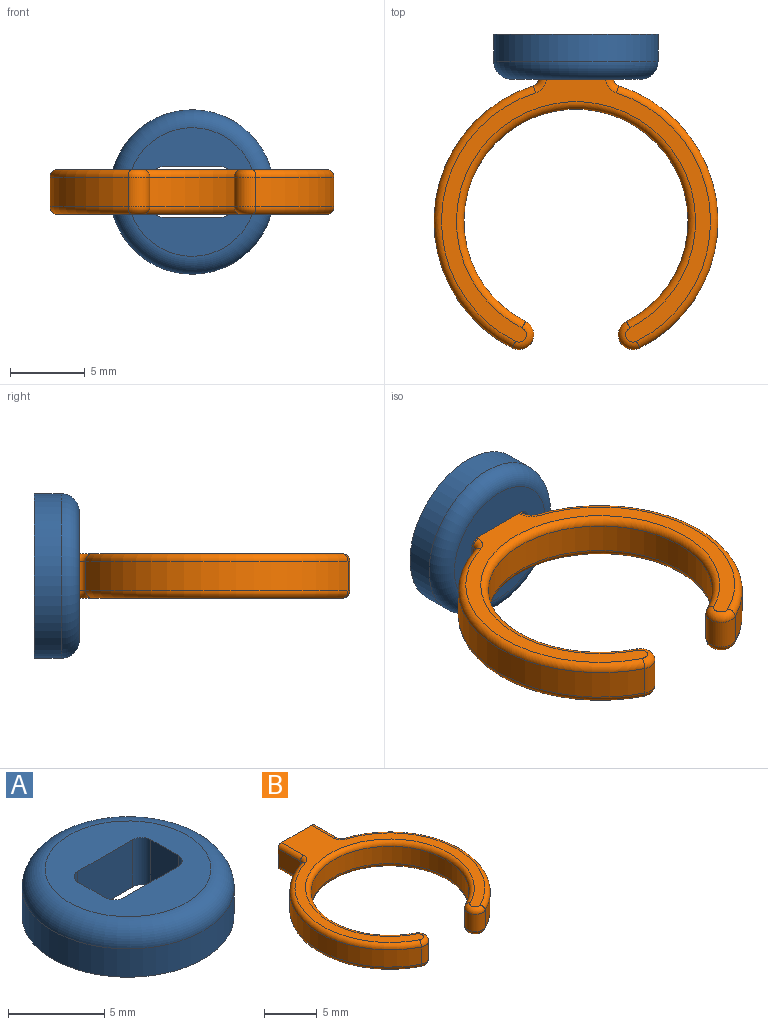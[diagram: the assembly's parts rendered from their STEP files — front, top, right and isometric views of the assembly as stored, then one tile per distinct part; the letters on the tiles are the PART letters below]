
ASSEMBLY  parts=2 mates=1
PART A: 12 faces, bbox 11.9x11.9x3 mm
  f0: plane 3x2mm, normal (1,0,0), area 6mm2, adj f5,f6,f8,f11
  f1: plane 4x3mm, normal (0,-1,0), area 12mm2, adj f5,f6,f8,f9
  f2: plane 3x2mm, normal (-1,0,0), area 6mm2, adj f5,f6,f9,f10
  f3: plane 4x3mm, normal (0,1,0), area 12mm2, adj f5,f6,f10,f11
  f4: cylinder r=5.5mm len=11mm, axis (0,0,-1), area 62.2mm2, adj f6,f7
  f5: plane 8.6x8.6mm, normal (0,0,1), area 40.5mm2, adj f0,f1,f2,f3,f7,f8,f9,f10
  f6: plane 11x11mm, normal (0,0,-1), area 77.4mm2, adj f0,f1,f2,f3,f4,f8,f9,f10
  f7: torus R=4.3mm, axis (0,0,1), area 60mm2, adj f4,f5
  f8: cylinder r=0.68mm len=3mm, axis (0,0,-1), area 3.2mm2, adj f0,f1,f5,f6
  f9: cylinder r=0.68mm len=3mm, axis (0,0,1), area 3.2mm2, adj f1,f2,f5,f6
  f10: cylinder r=0.68mm len=3mm, axis (0,0,-1), area 3.2mm2, adj f2,f3,f5,f6
  f11: cylinder r=0.68mm len=3mm, axis (0,0,1), area 3.2mm2, adj f0,f3,f5,f6
PART B: 30 faces, bbox 20.6x21.7x3 mm
  f0: plane 2.96x2mm, normal (-1,0,0), area 5.9mm2, adj f1,f7,f12,f21
  f1: cylinder r=0.5mm len=2mm, axis (0,0,-1), area 1.3mm2, adj f0,f2,f13,f22
  f2: cylinder r=9.5mm len=17.55mm, axis (0,0,-1), area 45mm2, adj f1,f10,f14,f23
  f3: cylinder r=7.5mm len=15mm, axis (0,0,-1), area 80.2mm2, adj f10,f11,f16,f25
  f4: cylinder r=9.5mm len=17.55mm, axis (0,0,-1), area 45mm2, adj f5,f11,f18,f27
  f5: cylinder r=0.5mm len=2mm, axis (0,0,-1), area 1.3mm2, adj f4,f6,f19,f28
  f6: plane 2.96x2mm, normal (1,0,0), area 5.9mm2, adj f5,f7,f20,f29
  f7: plane 5x3mm, normal (0,1,0), area 14.8mm2, adj f0,f6,f8,f9,f12,f20,f21,f29
  f8: plane 20.59x18mm, normal (0,0,1), area 60.8mm2, adj f7,f12,f13,f14,f15,f16,f17,f18
  f9: plane 20.59x18mm, normal (0,0,-1), area 60.8mm2, adj f7,f21,f22,f23,f24,f25,f26,f27
  f10: cylinder r=1mm len=2mm, axis (0,0,-1), area 6.3mm2, adj f2,f3,f15,f24
  f11: cylinder r=1mm len=2mm, axis (0,0,-1), area 6.3mm2, adj f3,f4,f17,f26
  f12: cylinder r=0.5mm len=2.96mm, axis (0,1,0), area 2.3mm2, adj f0,f7,f8,f13
  f13: torus R=1mm, axis (0,0,1), area 0.7mm2, adj f1,f8,f12,f14
  f14: torus R=9mm, axis (0,0,1), area 17.3mm2, adj f2,f8,f13,f15
  f15: torus R=0.5mm, axis (0,0,1), area 2mm2, adj f8,f10,f14,f16
  f16: torus R=8mm, axis (0,0,1), area 32.3mm2, adj f3,f8,f15,f17
  f17: torus R=0.5mm, axis (0,0,1), area 2mm2, adj f8,f11,f16,f18
  f18: torus R=9mm, axis (0,0,1), area 17.3mm2, adj f4,f8,f17,f19
  f19: torus R=1mm, axis (0,0,1), area 0.7mm2, adj f5,f8,f18,f20
  f20: cylinder r=0.5mm len=2.96mm, axis (0,-1,0), area 2.3mm2, adj f6,f7,f8,f19
  f21: cylinder r=0.5mm len=2.96mm, axis (0,-1,0), area 2.3mm2, adj f0,f7,f9,f22
  f22: torus R=1mm, axis (0,0,1), area 0.7mm2, adj f1,f9,f21,f23
  f23: torus R=9mm, axis (0,0,1), area 17.3mm2, adj f2,f9,f22,f24
  f24: torus R=0.5mm, axis (0,0,1), area 2mm2, adj f9,f10,f23,f25
  f25: torus R=8mm, axis (0,0,1), area 32.3mm2, adj f3,f9,f24,f26
  f26: torus R=0.5mm, axis (0,0,1), area 2mm2, adj f9,f11,f25,f27
  f27: torus R=9mm, axis (0,0,1), area 17.3mm2, adj f4,f9,f26,f28
  f28: torus R=1mm, axis (0,0,1), area 0.7mm2, adj f5,f9,f27,f29
  f29: cylinder r=0.5mm len=2.96mm, axis (0,1,0), area 2.3mm2, adj f6,f7,f9,f28
PLACE A rot(axis=(0,-0.71,0.71),180deg) t=(0,12.5,21.79)mm
PLACE B at identity fixed
MATE fastened A.f4 <-> B.f7  axis (0,1,0) through (0,12.5,1.5)mm
